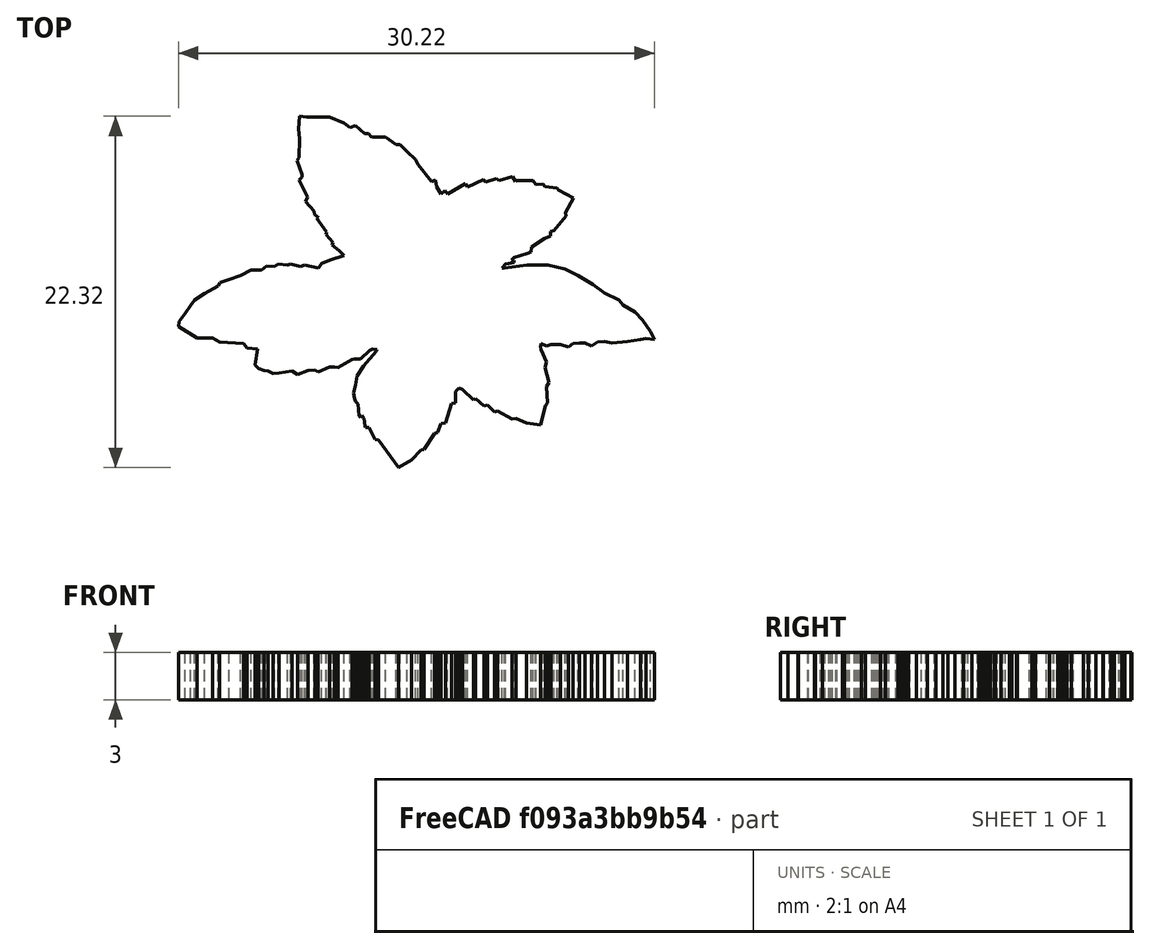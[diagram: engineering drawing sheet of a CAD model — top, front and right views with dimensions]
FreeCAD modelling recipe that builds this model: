
FCSTD DOCUMENT  (FreeCAD 0.20R29177 +233 (Git))
Label: mintsLeafLogo
License: All rights reserved
LicenseURL: http://en.wikipedia.org/wiki/All_rights_reserved
objects: Image::ImagePlane×1, Sketcher::SketchObject×1, PartDesign::Pad×1, PartDesign::Body×1
note: 4 computed .brp shape members not serialized (recipe doc carries the construction recipe); baked Part::Feature solids carry a one-line shape summary decoded from their .brp

FEATURE [Image::ImagePlane] ImagePlane
  XSize = 33.2103
  YSize = 25.9888
FEATURE [Sketcher::SketchObject] Sketch
  FullyConstrained = false
  MapMode = 5
  Support = -> [XY_Plane]
  sketch-geometry (197):
    g0: LineSegment StartX=-14.9397 StartY=-2.92245 StartZ=0 EndX=-13.7749 EndY=-3.63725 EndZ=0
    g1: LineSegment StartX=-13.7749 StartY=-3.63725 StartZ=0 EndX=-12.7689 EndY=-3.63725 EndZ=0
    g2: LineSegment StartX=-12.7689 StartY=-3.63725 StartZ=0 EndX=-12.3188 EndY=-3.90198 EndZ=0
    g3: LineSegment StartX=-12.3188 StartY=-3.90198 StartZ=0 EndX=-10.8098 EndY=-4.00788 EndZ=0
    g4: LineSegment StartX=-10.8098 StartY=-4.00788 StartZ=0 EndX=-10.5716 EndY=-4.29909 EndZ=0
    g5: LineSegment StartX=-10.5716 StartY=-4.29909 StartZ=0 EndX=-9.90971 EndY=-4.35204 EndZ=0
    g6: LineSegment StartX=-9.90971 StartY=-4.35204 StartZ=0 EndX=-10.0728 EndY=-5.35899 EndZ=0
    g7: LineSegment StartX=-10.0728 StartY=-5.35899 StartZ=0 EndX=-9.846 EndY=-5.60224 EndZ=0
    g8: LineSegment StartX=-9.846 StartY=-5.60224 StartZ=0 EndX=-9.51656 EndY=-5.73022 EndZ=0
    g9: LineSegment StartX=-9.51656 StartY=-5.73022 StartZ=0 EndX=-9.24931 EndY=-5.76229 EndZ=0
    g10: LineSegment StartX=-9.24931 StartY=-5.76229 StartZ=0 EndX=-8.92861 EndY=-5.90126 EndZ=0
    g11: LineSegment StartX=-8.92861 StartY=-5.90126 StartZ=0 EndX=-8.54378 EndY=-5.86384 EndZ=0
    g12: LineSegment StartX=-8.54378 StartY=-5.86384 StartZ=0 EndX=-7.71788 EndY=-5.75845 EndZ=0
    g13: LineSegment StartX=-7.71788 StartY=-5.75845 StartZ=0 EndX=-7.37291 EndY=-5.97257 EndZ=0
    g14: LineSegment StartX=-7.37291 StartY=-5.97257 StartZ=0 EndX=-6.72487 EndY=-5.72038 EndZ=0
    g15: LineSegment StartX=-6.72487 StartY=-5.72038 StartZ=0 EndX=-6.27066 EndY=-5.69481 EndZ=0
    g16: LineSegment StartX=-6.27066 StartY=-5.69481 StartZ=0 EndX=-6.06223 EndY=-5.80493 EndZ=0
    g17: LineSegment StartX=-6.06223 StartY=-5.80493 StartZ=0 EndX=-5.35089 EndY=-5.48914 EndZ=0
    g18: LineSegment StartX=-5.35089 StartY=-5.48914 StartZ=0 EndX=-5.02402 EndY=-5.48914 EndZ=0
    g19: LineSegment StartX=-5.02402 StartY=-5.48914 StartZ=0 EndX=-4.80126 EndY=-5.53132 EndZ=0
    g20: LineSegment StartX=-4.80126 StartY=-5.53132 StartZ=0 EndX=-3.91138 EndY=-5.02833 EndZ=0
    g21: LineSegment StartX=-3.91138 StartY=-5.02833 StartZ=0 EndX=-3.75191 EndY=-4.97251 EndZ=0
    g22: LineSegment StartX=-3.75191 StartY=-4.97251 StartZ=0 EndX=-3.37714 EndY=-4.97251 EndZ=0
    g23: LineSegment StartX=-3.37714 StartY=-4.97251 StartZ=0 EndX=-2.81898 EndY=-4.45422 EndZ=0
    g24: LineSegment StartX=-2.81898 StartY=-4.45422 StartZ=0 EndX=-2.62761 EndY=-4.34259 EndZ=0
    g25: LineSegment StartX=-2.62761 StartY=-4.34259 StartZ=0 EndX=-2.34055 EndY=-4.38246 EndZ=0
    g26: LineSegment StartX=-2.34055 StartY=-4.38246 StartZ=0 EndX=-2.38042 EndY=-4.51801 EndZ=0
    g27: LineSegment StartX=-2.38042 StartY=-4.51801 StartZ=0 EndX=-3.18577 EndY=-5.42702 EndZ=0
    g28: LineSegment StartX=-3.18577 StartY=-5.42702 StartZ=0 EndX=-3.61318 EndY=-6.05824 EndZ=0
    g29: LineSegment StartX=-3.61318 StartY=-6.05824 StartZ=0 EndX=-3.7111 EndY=-6.64579 EndZ=0
    g30: LineSegment StartX=-3.7111 StartY=-6.64579 StartZ=0 EndX=-3.83514 EndY=-7.15501 EndZ=0
    g31: LineSegment StartX=-3.83514 StartY=-7.15501 StartZ=0 EndX=-3.75878 EndY=-7.50876 EndZ=0
    g32: LineSegment StartX=-3.75878 StartY=-7.50876 StartZ=0 EndX=-3.70596 EndY=-7.68135 EndZ=0
    g33: LineSegment StartX=-3.70596 StartY=-7.68135 StartZ=0 EndX=-3.53967 EndY=-7.85202 EndZ=0
    g34: LineSegment StartX=-3.53967 StartY=-7.85202 StartZ=0 EndX=-3.48159 EndY=-8.61241 EndZ=0
    g35: LineSegment StartX=-3.48159 StartY=-8.61241 StartZ=0 EndX=-3.39019 EndY=-8.69728 EndZ=0
    g36: LineSegment StartX=-3.39019 StartY=-8.69728 StartZ=0 EndX=-3.27268 EndY=-8.56671 EndZ=0
    g37: LineSegment StartX=-3.27268 StartY=-8.56671 StartZ=0 EndX=-3.16823 EndY=-8.76909 EndZ=0
    g38: LineSegment StartX=-3.16823 StartY=-8.76909 StartZ=0 EndX=-3.10294 EndY=-9.25219 EndZ=0
    g39: LineSegment StartX=-3.10294 StartY=-9.25219 StartZ=0 EndX=-3.07088 EndY=-9.32083 EndZ=0
    g40: LineSegment StartX=-3.07088 StartY=-9.32083 StartZ=0 EndX=-2.84207 EndY=-9.3355 EndZ=0
    g41: LineSegment StartX=-2.84207 StartY=-9.3355 StartZ=0 EndX=-2.45193 EndY=-10.0982 EndZ=0
    g42: LineSegment StartX=-2.45193 StartY=-10.0982 StartZ=0 EndX=-2.24953 EndY=-10.1304 EndZ=0
    g43: LineSegment StartX=-2.24953 StartY=-10.1304 StartZ=0 EndX=-0.96042 EndY=-11.8753 EndZ=0
    g44: LineSegment StartX=-0.96042 StartY=-11.8753 StartZ=0 EndX=-0.153326 EndY=-11.3889 EndZ=0
    g45: LineSegment StartX=-0.153326 StartY=-11.3889 StartZ=0 EndX=0.461347 EndY=-10.7689 EndZ=0
    g46: LineSegment StartX=0.461347 StartY=-10.7689 StartZ=0 EndX=0.669802 EndY=-10.7261 EndZ=0
    g47: LineSegment StartX=0.669802 StartY=-10.7261 StartZ=0 EndX=1.31724 EndY=-9.70998 EndZ=0
    g48: LineSegment StartX=1.31724 StartY=-9.70998 StartZ=0 EndX=1.51826 EndY=-9.65081 EndZ=0
    g49: LineSegment StartX=1.51826 StartY=-9.65081 StartZ=0 EndX=1.74022 EndY=-9.08937 EndZ=0
    g50: LineSegment StartX=1.74022 StartY=-9.08937 StartZ=0 EndX=2.02094 EndY=-9.04367 EndZ=0
    g51: LineSegment StartX=2.02094 StartY=-9.04367 StartZ=0 EndX=2.39306 EndY=-7.80327 EndZ=0
    g52: LineSegment StartX=2.39306 StartY=-7.80327 StartZ=0 EndX=2.6542 EndY=-7.77716 EndZ=0
    g53: LineSegment StartX=2.6542 StartY=-7.77716 StartZ=0 EndX=2.6542 EndY=-7.03945 EndZ=0
    g54: LineSegment StartX=2.6542 StartY=-7.03945 StartZ=0 EndX=2.86963 EndY=-6.81749 EndZ=0
    g55: LineSegment StartX=2.86963 StartY=-6.81749 StartZ=0 EndX=3.0916 EndY=-6.92847 EndZ=0
    g56: LineSegment StartX=3.0916 StartY=-6.92847 StartZ=0 EndX=3.79666 EndY=-7.57478 EndZ=0
    g57: LineSegment StartX=3.79666 StartY=-7.57478 StartZ=0 EndX=3.93376 EndY=-7.50297 EndZ=0
    g58: LineSegment StartX=3.93376 StartY=-7.50297 StartZ=0 EndX=4.46256 EndY=-7.97301 EndZ=0
    g59: LineSegment StartX=4.46256 StartY=-7.97301 StartZ=0 EndX=4.68452 EndY=-7.92079 EndZ=0
    g60: LineSegment StartX=4.68452 StartY=-7.92079 StartZ=0 EndX=5.1154 EndY=-8.34513 EndZ=0
    g61: LineSegment StartX=5.1154 StartY=-8.34513 StartZ=0 EndX=5.32431 EndY=-8.28637 EndZ=0
    g62: LineSegment StartX=5.32431 StartY=-8.28637 StartZ=0 EndX=6.23668 EndY=-8.79564 EndZ=0
    g63: LineSegment StartX=6.23668 StartY=-8.79564 StartZ=0 EndX=6.50362 EndY=-8.76631 EndZ=0
    g64: LineSegment StartX=6.50362 StartY=-8.76631 StartZ=0 EndX=7.14802 EndY=-9.05537 EndZ=0
    g65: LineSegment StartX=7.14802 StartY=-9.05537 StartZ=0 EndX=8.04883 EndY=-9.18613 EndZ=0
    g66: LineSegment StartX=8.04883 StartY=-9.18613 StartZ=0 EndX=8.36847 EndY=-7.93662 EndZ=0
    g67: LineSegment StartX=8.36847 StartY=-7.93662 StartZ=0 EndX=8.49923 EndY=-7.79133 EndZ=0
    g68: LineSegment StartX=8.49923 StartY=-7.79133 StartZ=0 EndX=8.43477 EndY=-6.72206 EndZ=0
    g69: LineSegment StartX=8.43477 StartY=-6.72206 StartZ=0 EndX=8.58621 EndY=-6.47988 EndZ=0
    g70: LineSegment StartX=8.58621 StartY=-6.47988 StartZ=0 EndX=8.32296 EndY=-5.53178 EndZ=0
    g71: LineSegment StartX=8.32296 StartY=-5.53178 StartZ=0 EndX=8.43984 EndY=-5.19091 EndZ=0
    g72: LineSegment StartX=8.43984 StartY=-5.19091 StartZ=0 EndX=8.07426 EndY=-4.39307 EndZ=0
    g73: LineSegment StartX=8.07426 StartY=-4.39307 StartZ=0 EndX=8.04236 EndY=-4.17777 EndZ=0
    g74: LineSegment StartX=8.04236 StartY=-4.17777 StartZ=0 EndX=8.0902 EndY=-3.99438 EndZ=0
    g75: LineSegment StartX=8.0902 StartY=-3.99438 StartZ=0 EndX=8.43308 EndY=-4.1698 EndZ=0
    g76: LineSegment StartX=8.43308 StartY=-4.1698 StartZ=0 EndX=8.72013 EndY=-4.0502 EndZ=0
    g77: LineSegment StartX=8.72013 StartY=-4.0502 StartZ=0 EndX=9.31817 EndY=-4.0502 EndZ=0
    g78: LineSegment StartX=9.31817 StartY=-4.0502 StartZ=0 EndX=9.82052 EndY=-4.21764 EndZ=0
    g79: LineSegment StartX=9.82052 StartY=-4.21764 StartZ=0 EndX=10.1323 EndY=-4.01453 EndZ=0
    g80: LineSegment StartX=10.1323 StartY=-4.01453 StartZ=0 EndX=10.5175 EndY=-3.9623 EndZ=0
    g81: LineSegment StartX=10.5175 StartY=-3.9623 StartZ=0 EndX=10.8831 EndY=-3.97536 EndZ=0
    g82: LineSegment StartX=10.8831 StartY=-3.97536 StartZ=0 EndX=11.2878 EndY=-4.15815 EndZ=0
    g83: LineSegment StartX=11.2878 StartY=-4.15815 StartZ=0 EndX=11.6861 EndY=-3.91007 EndZ=0
    g84: LineSegment StartX=11.6861 StartY=-3.91007 StartZ=0 EndX=12.1039 EndY=-3.88396 EndZ=0
    g85: LineSegment StartX=12.1039 StartY=-3.88396 StartZ=0 EndX=12.6 EndY=-3.9623 EndZ=0
    g86: LineSegment StartX=12.6 StartY=-3.9623 StartZ=0 EndX=13.5793 EndY=-3.87743 EndZ=0
    g87: LineSegment StartX=13.5793 StartY=-3.87743 StartZ=0 EndX=14.3888 EndY=-3.74687 EndZ=0
    g88: LineSegment StartX=14.3888 StartY=-3.74687 StartZ=0 EndX=14.7544 EndY=-3.68158 EndZ=0
    g89: LineSegment StartX=14.7544 StartY=-3.68158 StartZ=0 EndX=15.2767 EndY=-3.75339 EndZ=0
    g90: LineSegment StartX=15.2767 StartY=-3.75339 StartZ=0 EndX=15.0432 EndY=-3.24137 EndZ=0
    g91: LineSegment StartX=15.0432 StartY=-3.24137 StartZ=0 EndX=14.5209 EndY=-2.51672 EndZ=0
    g92: LineSegment StartX=14.5209 StartY=-2.51672 StartZ=0 EndX=14.0378 EndY=-1.99445 EndZ=0
    g93: LineSegment StartX=14.0378 StartY=-1.99445 StartZ=0 EndX=13.2802 EndY=-1.54625 EndZ=0
    g94: LineSegment StartX=13.2802 StartY=-1.54625 StartZ=0 EndX=13.0438 EndY=-1.23117 EndZ=0
    g95: LineSegment StartX=13.0438 StartY=-1.23117 StartZ=0 EndX=12.1074 EndY=-0.797939 EndZ=0
    g96: LineSegment StartX=12.1074 StartY=-0.797939 StartZ=0 EndX=11.3804 EndY=-0.250878 EndZ=0
    g97: LineSegment StartX=11.3804 StartY=-0.250878 StartZ=0 EndX=10.4396 EndY=0.304889 EndZ=0
    g98: LineSegment StartX=10.4396 StartY=0.304889 StartZ=0 EndX=9.59526 EndY=0.727998 EndZ=0
    g99: LineSegment StartX=9.59526 StartY=0.727998 StartZ=0 EndX=8.53624 EndY=0.97306 EndZ=0
    g100: LineSegment StartX=8.53624 StartY=0.97306 StartZ=0 EndX=7.199 EndY=0.97306 EndZ=0
    g101: LineSegment StartX=7.199 StartY=0.97306 StartZ=0 EndX=5.77932 EndY=0.795578 EndZ=0
    g102: LineSegment StartX=5.77932 StartY=0.795578 StartZ=0 EndX=5.60186 EndY=0.795578 EndZ=0
    g103: LineSegment StartX=5.60186 StartY=0.795578 StartZ=0 EndX=5.83256 EndY=1.06177 EndZ=0
    g104: LineSegment StartX=5.83256 StartY=1.06177 StartZ=0 EndX=6.38268 EndY=1.13275 EndZ=0
    g105: LineSegment StartX=6.38268 StartY=1.13275 StartZ=0 EndX=6.38268 EndY=1.25697 EndZ=0
    g106: LineSegment StartX=6.38268 StartY=1.25697 StartZ=0 EndX=6.21713 EndY=1.313 EndZ=0
    g107: LineSegment StartX=6.21713 StartY=1.313 StartZ=0 EndX=6.37904 EndY=1.46617 EndZ=0
    g108: LineSegment StartX=6.37904 StartY=1.46617 StartZ=0 EndX=7.17987 EndY=1.70686 EndZ=0
    g109: LineSegment StartX=7.17987 StartY=1.70686 StartZ=0 EndX=7.44682 EndY=1.79438 EndZ=0
    g110: LineSegment StartX=7.44682 StartY=1.79438 StartZ=0 EndX=7.49058 EndY=2.12696 EndZ=0
    g111: LineSegment StartX=7.49058 StartY=2.12696 StartZ=0 EndX=8.30058 EndY=2.66839 EndZ=0
    g112: LineSegment StartX=8.30058 StartY=2.66839 StartZ=0 EndX=8.68575 EndY=2.81854 EndZ=0
    g113: LineSegment StartX=8.68575 StartY=2.81854 StartZ=0 EndX=8.68575 EndY=3.12537 EndZ=0
    g114: LineSegment StartX=8.68575 StartY=3.12537 StartZ=0 EndX=8.89508 EndY=3.18684 EndZ=0
    g115: LineSegment StartX=8.89508 StartY=3.18684 StartZ=0 EndX=9.66534 EndY=4.09369 EndZ=0
    g116: LineSegment StartX=9.66534 StartY=4.09369 StartZ=0 EndX=9.62638 EndY=4.32743 EndZ=0
    g117: LineSegment StartX=9.62638 StartY=4.32743 StartZ=0 EndX=10.1426 EndY=5.22344 EndZ=0
    g118: LineSegment StartX=10.1426 StartY=5.22344 StartZ=0 EndX=9.19786 EndY=5.7591 EndZ=0
    g119: LineSegment StartX=9.19786 StartY=5.7591 StartZ=0 EndX=9.1102 EndY=5.87597 EndZ=0
    g120: LineSegment StartX=9.1102 StartY=5.87597 StartZ=0 EndX=8.32132 EndY=5.97336 EndZ=0
    g121: LineSegment StartX=8.32132 StartY=5.97336 StartZ=0 EndX=8.20531 EndY=6.14025 EndZ=0
    g122: LineSegment StartX=8.20531 StartY=6.14025 StartZ=0 EndX=7.75633 EndY=6.09749 EndZ=0
    g123: LineSegment StartX=7.71892 StartY=6.13491 StartZ=0 EndX=7.56391 EndY=6.33267 EndZ=0
    g124: LineSegment StartX=7.56391 StartY=6.33267 StartZ=0 EndX=6.52164 EndY=6.33267 EndZ=0
    g125: LineSegment StartX=6.52164 StartY=6.33267 StartZ=0 EndX=6.46819 EndY=6.29526 EndZ=0
    g126: LineSegment StartX=6.46819 StartY=6.29526 StartZ=0 EndX=6.27042 EndY=6.61061 EndZ=0
    g127: LineSegment StartX=6.27042 StartY=6.61061 StartZ=0 EndX=5.40453 EndY=6.33267 EndZ=0
    g128: LineSegment StartX=5.40453 StartY=6.33267 StartZ=0 EndX=5.27091 EndY=6.47164 EndZ=0
    g129: LineSegment StartX=5.27091 StartY=6.47164 StartZ=0 EndX=4.56942 EndY=6.24725 EndZ=0
    g130: LineSegment StartX=4.56942 StartY=6.24725 StartZ=0 EndX=4.44161 EndY=6.40652 EndZ=0
    g131: LineSegment StartX=4.44161 StartY=6.40652 StartZ=0 EndX=3.4195 EndY=5.94588 EndZ=0
    g132: LineSegment StartX=3.4195 StartY=5.94588 StartZ=0 EndX=3.29192 EndY=6.1532 EndZ=0
    g133: LineSegment StartX=3.29192 StartY=6.1532 StartZ=0 EndX=2.15964 EndY=5.49137 EndZ=0
    g134: LineSegment StartX=2.15964 StartY=5.49137 StartZ=0 EndX=2.00016 EndY=5.69869 EndZ=0
    g135: LineSegment StartX=2.00016 StartY=5.69869 StartZ=0 EndX=1.72905 EndY=5.47543 EndZ=0
    g136: LineSegment StartX=1.72905 StartY=5.47543 StartZ=0 EndX=1.46239 EndY=5.95187 EndZ=0
    g137: LineSegment StartX=1.46239 StartY=5.95187 StartZ=0 EndX=1.39073 EndY=6.37823 EndZ=0
    g138: LineSegment StartX=1.39073 StartY=6.37823 StartZ=0 EndX=1.13993 EndY=6.27432 EndZ=0
    g139: LineSegment StartX=1.13993 StartY=6.27432 StartZ=0 EndX=0.283337 EndY=7.37871 EndZ=0
    g140: LineSegment StartX=0.283337 StartY=7.37871 StartZ=0 EndX=0.126706 EndY=7.68126 EndZ=0
    g141: LineSegment StartX=0.126706 StartY=7.68126 StartZ=0 EndX=-0.415308 EndY=8.18163 EndZ=0
    g142: LineSegment StartX=-0.415308 StartY=8.18163 StartZ=0 EndX=-0.872658 EndY=8.6237 EndZ=0
    g143: LineSegment StartX=-0.872658 StartY=8.6237 StartZ=0 EndX=-1.12074 EndY=8.64329 EndZ=0
    g144: LineSegment StartX=-1.12074 StartY=8.64329 StartZ=0 EndX=-1.79316 EndY=9.11986 EndZ=0
    g145: LineSegment StartX=-1.79316 StartY=9.11986 StartZ=0 EndX=-2.57005 EndY=9.11986 EndZ=0
    g146: LineSegment StartX=-2.57005 StartY=9.11986 StartZ=0 EndX=-2.71321 EndY=9.13846 EndZ=0
    g147: LineSegment StartX=-2.71321 StartY=9.13846 StartZ=0 EndX=-2.88425 EndY=9.34157 EndZ=0
    g148: LineSegment StartX=-2.88425 StartY=9.34157 StartZ=0 EndX=-3.11943 EndY=9.34157 EndZ=0
    g149: LineSegment StartX=-3.11943 StartY=9.34157 StartZ=0 EndX=-3.70739 EndY=9.82796 EndZ=0
    g150: LineSegment StartX=-3.70739 StartY=9.82796 StartZ=0 EndX=-4.04915 EndY=9.7003 EndZ=0
    g151: LineSegment StartX=-4.04915 StartY=9.7003 StartZ=0 EndX=-4.42988 EndY=10.011 EndZ=0
    g152: LineSegment StartX=-4.42988 StartY=10.011 StartZ=0 EndX=-5.35895 EndY=10.3845 EndZ=0
    g153: LineSegment StartX=-5.35895 StartY=10.3845 StartZ=0 EndX=-6.81188 EndY=10.3845 EndZ=0
    g154: LineSegment StartX=-6.81188 StartY=10.3845 StartZ=0 EndX=-7.2384 EndY=10.4407 EndZ=0
    g155: LineSegment StartX=-7.2384 StartY=10.4407 StartZ=0 EndX=-7.30788 EndY=9.63363 EndZ=0
    g156: LineSegment StartX=-7.30788 StartY=9.63363 StartZ=0 EndX=-7.25443 EndY=9.00826 EndZ=0
    g157: LineSegment StartX=-7.25443 StartY=9.00826 StartZ=0 EndX=-7.29297 EndY=7.81176 EndZ=0
    g158: LineSegment StartX=-7.29297 StartY=7.81176 StartZ=0 EndX=-7.41112 EndY=7.6042 EndZ=0
    g159: LineSegment StartX=-7.41112 StartY=7.6042 StartZ=0 EndX=-7.09216 EndY=6.74302 EndZ=0
    g160: LineSegment StartX=-7.09216 StartY=6.74302 StartZ=0 EndX=-7.10014 EndY=6.55962 EndZ=0
    g161: LineSegment StartX=-7.10014 StartY=6.55962 StartZ=0 EndX=-7.29151 EndY=6.3842 EndZ=0
    g162: LineSegment StartX=-7.29151 StartY=6.3842 StartZ=0 EndX=-6.74132 EndY=5.29976 EndZ=0
    g163: LineSegment StartX=-6.74132 StartY=5.29976 StartZ=0 EndX=-6.87495 EndY=5.02732 EndZ=0
    g164: LineSegment StartX=-6.87495 StartY=5.02732 StartZ=0 EndX=-6.31586 EndY=4.42065 EndZ=0
    g165: LineSegment StartX=-6.31586 StartY=4.42065 StartZ=0 EndX=-6.30396 EndY=4.19463 EndZ=0
    g166: LineSegment StartX=-6.30396 StartY=4.19463 StartZ=0 EndX=-6.05415 EndY=4.0043 EndZ=0
    g167: LineSegment StartX=-6.05415 StartY=4.0043 StartZ=0 EndX=-6.18501 EndY=3.95672 EndZ=0
    g168: LineSegment StartX=-6.18501 StartY=3.95672 StartZ=0 EndX=-5.54265 EndY=3.07645 EndZ=0
    g169: LineSegment StartX=-5.54265 StartY=3.07645 StartZ=0 EndX=-5.57833 EndY=2.90991 EndZ=0
    g170: LineSegment StartX=-5.57833 StartY=2.90991 StartZ=0 EndX=-5.1263 EndY=2.41029 EndZ=0
    g171: LineSegment StartX=-5.1263 StartY=2.41029 StartZ=0 EndX=-5.18578 EndY=2.26755 EndZ=0
    g172: LineSegment StartX=-5.18578 StartY=2.26755 StartZ=0 EndX=-4.73375 EndY=1.89878 EndZ=0
    g173: LineSegment StartX=-4.73375 StartY=1.89878 StartZ=0 EndX=-4.42446 EndY=1.5895 EndZ=0
    g174: LineSegment StartX=-4.42446 StartY=1.5895 StartZ=0 EndX=-5.31663 EndY=1.29211 EndZ=0
    g175: LineSegment StartX=-5.31663 StartY=1.29211 StartZ=0 EndX=-5.84004 EndY=1.08988 EndZ=0
    g176: LineSegment StartX=-5.84004 StartY=1.08988 StartZ=0 EndX=-6.04226 EndY=0.792495 EndZ=0
    g177: LineSegment StartX=-6.04226 StartY=0.792495 StartZ=0 EndX=-6.94632 EndY=0.994719 EndZ=0
    g178: LineSegment StartX=-6.94632 StartY=0.994719 StartZ=0 EndX=-7.19613 EndY=0.887659 EndZ=0
    g179: LineSegment StartX=-7.19613 StartY=0.887659 StartZ=0 EndX=-7.8147 EndY=1.0423 EndZ=0
    g180: LineSegment StartX=-7.8147 StartY=1.0423 StartZ=0 EndX=-8.02502 EndY=0.969153 EndZ=0
    g181: LineSegment StartX=-8.02502 StartY=0.969153 StartZ=0 EndX=-8.60267 EndY=1.03042 EndZ=0
    g182: LineSegment StartX=-8.60267 StartY=1.03042 StartZ=0 EndX=-8.8346 EndY=0.872878 EndZ=0
    g183: LineSegment StartX=-8.8346 StartY=0.872878 StartZ=0 EndX=-9.33349 EndY=0.929767 EndZ=0
    g184: LineSegment StartX=-9.33349 StartY=0.929767 StartZ=0 EndX=-9.66169 EndY=0.649695 EndZ=0
    g185: LineSegment StartX=-9.66169 StartY=0.649695 StartZ=0 EndX=-10.3249 EndY=0.649695 EndZ=0
    g186: LineSegment StartX=-10.3249 StartY=0.649695 StartZ=0 EndX=-11.0107 EndY=0.32425 EndZ=0
    g187: LineSegment StartX=-11.0107 StartY=0.32425 StartZ=0 EndX=-11.7283 EndY=0.053139 EndZ=0
    g188: LineSegment StartX=-11.7283 StartY=0.053139 StartZ=0 EndX=-12.2971 EndY=-0.13161 EndZ=0
    g189: LineSegment StartX=-12.2971 StartY=-0.13161 StartZ=0 EndX=-12.4212 EndY=-0.347049 EndZ=0
    g190: LineSegment StartX=-12.4212 StartY=-0.347049 StartZ=0 EndX=-13.296 EndY=-0.817096 EndZ=0
    g191: LineSegment StartX=-13.296 StartY=-0.817096 StartZ=0 EndX=-13.9227 EndY=-1.24144 EndZ=0
    g192: LineSegment StartX=-13.9227 StartY=-1.24144 StartZ=0 EndX=-14.1708 EndY=-1.59398 EndZ=0
    g193: LineSegment StartX=-14.1708 StartY=-1.59398 StartZ=0 EndX=-14.5386 EndY=-2.09216 EndZ=0
    g194: LineSegment StartX=-14.5386 StartY=-2.09216 StartZ=0 EndX=-14.8974 EndY=-2.61843 EndZ=0
    g195: LineSegment StartX=-14.8974 StartY=-2.61843 StartZ=0 EndX=-14.9397 EndY=-2.92245 EndZ=0
    g196: LineSegment StartX=7.75633 StartY=6.09749 StartZ=0 EndX=7.71892 EndY=6.13491 EndZ=0
  constraints (88):
    c: Coincident(g1,g0)
    c: Coincident(g2,g1)
    c: Coincident(g3,g2)
    c: Coincident(g6,g5)
    c: Coincident(g7,g6)
    c: Coincident(g8,g7)
    c: Coincident(g9,g8)
    c: Coincident(g10,g9)
    c: Coincident(g12,g11)
    c: Coincident(g13,g12)
    c: Coincident(g14,g13)
    c: Coincident(g15,g14)
    c: Coincident(g17,g16)
    c: Coincident(g20,g19)
    c: Coincident(g28,g27)
    c: Coincident(g31,g30)
    c: Coincident(g32,g31)
    c: Coincident(g34,g33)
    c: Coincident(g39,g38)
    c: Coincident(g43,g42)
    c: Coincident(g47,g46)
    c: Coincident(g48,g47)
    c: Coincident(g50,g49)
    c: Coincident(g55,g54)
    c: Coincident(g62,g61)
    c: Coincident(g63,g62)
    c: Coincident(g68,g67)
    c: Coincident(g69,g68)
    c: Coincident(g70,g69)
    c: Coincident(g72,g71)
    c: Coincident(g74,g73)
    c: Coincident(g78,g77)
    c: Coincident(g79,g78)
    c: Coincident(g83,g82)
    c: Coincident(g85,g84)
    c: Coincident(g86,g85)
    c: Coincident(g87,g86)
    c: Coincident(g90,g89)
    c: Coincident(g93,g92)
    c: Coincident(g94,g93)
    c: Coincident(g96,g95)
    c: Coincident(g98,g97)
    c: Coincident(g99,g98)
    c: Coincident(g100,g99)
    c: Coincident(g102,g101)
    c: Coincident(g103,g102)
    c: Coincident(g104,g103)
    c: Coincident(g106,g105)
    c: Coincident(g108,g107)
    c: Coincident(g109,g108)
    c: Coincident(g111,g110)
    c: Coincident(g113,g112)
    c: Coincident(g114,g113)
    c: Coincident(g115,g114)
    c: Coincident(g116,g115)
    c: Coincident(g119,g118)
    c: Coincident(g121,g120)
    c: Coincident(g124,g123)
    c: Coincident(g125,g124)
    c: Coincident(g129,g128)
    c: Coincident(g131,g130)
    c: Coincident(g136,g135)
    c: Coincident(g139,g138)
    c: Coincident(g140,g139)
    c: Coincident(g142,g141)
    c: Coincident(g146,g145)
    c: Coincident(g150,g149)
    c: Coincident(g151,g150)
    c: Coincident(g152,g151)
    c: Coincident(g154,g153)
    c: Coincident(g156,g155)
    c: Coincident(g157,g156)
    c: Coincident(g158,g157)
    c: Coincident(g159,g158)
    c: Coincident(g163,g162)
    c: Coincident(g166,g165)
    c: Coincident(g180,g179)
    c: Coincident(g181,g180)
    c: Coincident(g183,g182)
    c: Coincident(g185,g184)
    c: Coincident(g188,g187)
    c: Coincident(g189,g188)
    c: Coincident(g192,g191)
    c: Coincident(g193,g192)
    c: Coincident(g195,g194)
    c: Coincident(g195,g0)
    c: Coincident(g196,g122)
    c: Coincident(g196,g123)
FEATURE [PartDesign::Pad] Pad
  Direction = (0,0,1)
  Length = 3
  Length2 = 10
  Profile = -> Sketch
  ReferenceAxis = -> Sketch [N_Axis]
  Type = 0
FEATURE [PartDesign::Body] Body
  Group = -> [Sketch,Pad]
  Origin = -> Origin
  Tip = -> Pad
